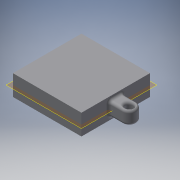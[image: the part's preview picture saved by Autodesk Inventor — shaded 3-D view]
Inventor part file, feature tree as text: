
AUTODESK INVENTOR PART (.ipt)
format: ipt  version: 2019 (Build 230136000, 136)  size: 153,600 bytes
history: native  units: mm
features: sketch x3, extrude x2, plane x1, hole x1, fillet x1
ambient origin geometry x8: Origin, YZ Plane, XZ Plane, XY Plane, X Axis, Y Axis, Z Axis, Center Point
bodies: Solid1 (feature_tree)
feature tree (8):
  extrude  "Extrusion1"  Depth=50.0mm
  plane  "Work Plane1"
  extrude  "Extrusion2"  Depth=10.0mm
  hole  "Hole1"  [1 undecoded]
  fillet  "Fillet1"  Radius=2.0mm
  sketch  "Sketch1"  dims[d0=50.0mm d1=50.0mm]
  sketch  "Sketch2"  dims[d2=15.0mm d3=0.0mm d4=10.0mm]
  sketch  "Sketch3"  dims[d5=10.0mm d6=10.0mm d7=0.0mm d8=5.5mm d9=6.0mm d10=10.4mm d11=2.0mm d12=90.0deg d13=8.0mm d14=20.594885mm d15=2.0mm]
note: 1 required parameter value undecoded (feature->parameter linkage not recoverable at this tier; creation-order binding heuristic only, values carry confidence <= 0.55)
